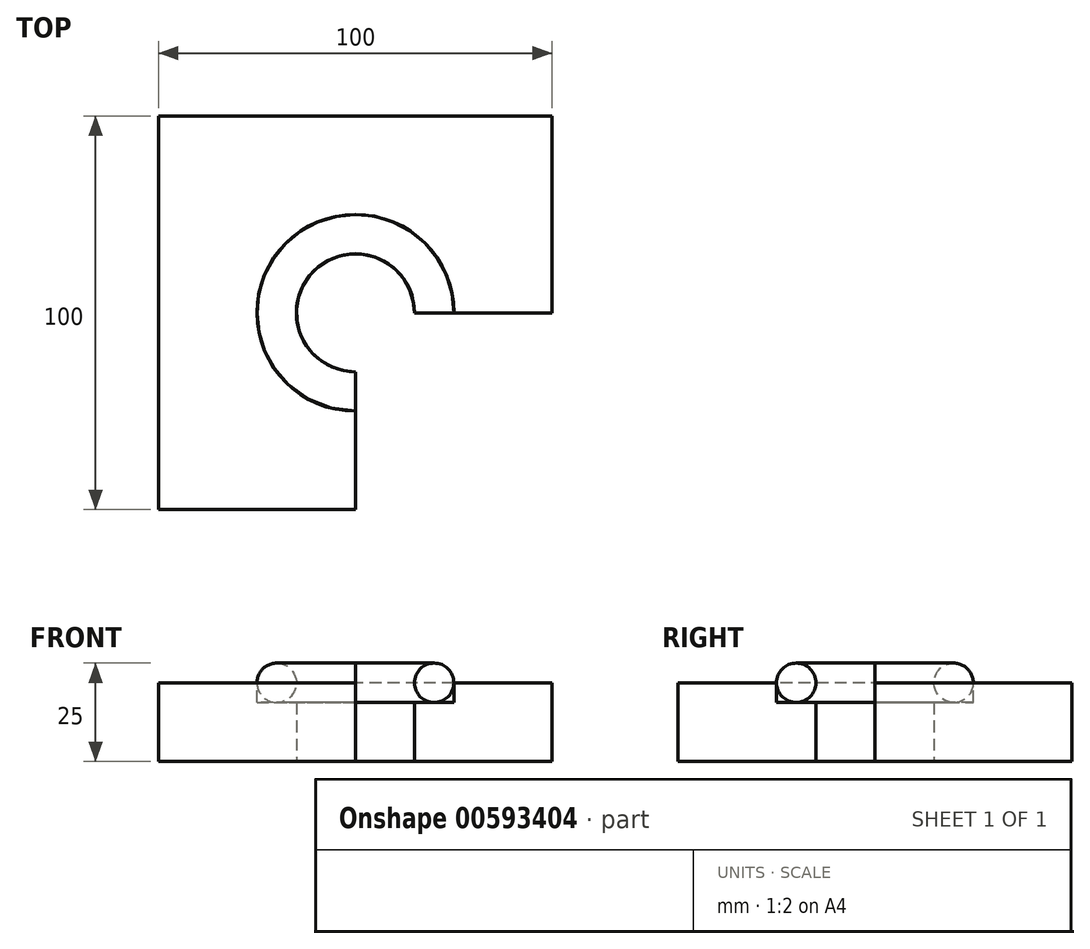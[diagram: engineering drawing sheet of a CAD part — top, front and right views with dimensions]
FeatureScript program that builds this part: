
annotation { "Feature Type Name" : "Feature", "Feature Type Description" : "" }
export const myFeature = defineFeature(function(context is Context, id is Id, definition is map)
    precondition{}
    {
        {
            var Q0;
            Q0=qCreatedBy(makeId("Top.planeOp"),FACE);
            var sketch = newSketch(context, id + "F0", { "sketchPlane" : qUnion([Q0])});
            skLineSegment(sketch, "E0.bottom", {"start": v(-50, 50) * mm, "end": v(50, 50) * mm});
            skLineSegment(sketch, "E0.top", {"start": v(-50, -50) * mm, "end": v(50, -50) * mm});
            skLineSegment(sketch, "E0.left", {"start": v(-50, 50) * mm, "end": v(-50, -50) * mm});
            skLineSegment(sketch, "E0.right", {"start": v(50, 50) * mm, "end": v(50, -50) * mm});
            skPoint(sketch, "E0.middle", {"position": v(0, 0) * mm});
            skCircle(sketch, "E1", {"center": v(0, 0) * mm, "radius": 15 * mm});
            skSolve(sketch);
        }
        {
            var Q0;
            Q0=makeQuery(id+"F0.imprint","IMPRINT",FACE,{"disambiguationData":[TD([[makeQuery(id+"F0.imprint","IMPRINT",EDGE,{"derivedFrom":sQuery(id+"F0.wireOp",EDGE,"E0.bottom")}),-1.0]])]});
            extrude(context, id + "F1", {"entities" : qUnion([Q0]), "depth" : 20 * mm, "offsetDistance" : 25 * mm});
        }
        {
            var Q0;
            Q0=makeQuery(id+"F1.opExtrude","CAP_FACE",FACE,{"disambiguationData":[OSD([sQuery(id+"F0.wireOp",EDGE,"E0.bottom"),sQuery(id+"F0.wireOp",EDGE,"E0.top"),sQuery(id+"F0.wireOp",EDGE,"E0.left"),sQuery(id+"F0.wireOp",EDGE,"E0.right"),sQuery(id+"F0.wireOp",EDGE,"E1")])],"isStart":false});
            var sketch = newSketch(context, id + "F2", { "sketchPlane" : qUnion([Q0])});
            skCircle(sketch, "E2", {"center": v(0, 0) * mm, "radius": 25 * mm});
            skSolve(sketch);
        }
        {
            var Q0;
            Q0=makeQuery(id+"F2.imprint","IMPRINT",FACE,{"disambiguationData":[TD([[makeQuery(id+"F2.imprint","IMPRINT",EDGE,{"derivedFrom":sQuery(id+"F2.wireOp",EDGE,"E2")}),1.0]])]});
            extrude(context, id + "F3", {"entities" : qUnion([Q0]), "operationType" : NewBodyOperationType.REMOVE, "oppositeDirection" : true, "depth" : 5 * mm, "offsetDistance" : 25 * mm});
        }
        {
            var Q0;
            Q0=qCreatedBy(makeId("Front.planeOp"),FACE);
            var sketch = newSketch(context, id + "F4", { "sketchPlane" : qUnion([Q0])});
            skCircle(sketch, "E3", {"center": v(-20, 20) * mm, "radius": 5 * mm});
            skSolve(sketch);
        }
        {
            var Q0;
            Q0 = qSketchRegion(id + "F4", true);
            var Q1;
            Q1=makeQuery(id+"F1.opExtrude","SWEPT_FACE",FACE,{"disambiguationData":[OSD([sQuery(id+"F0.wireOp",EDGE,"E1")])]});
            revolve(context, id + "F5", {"surfaceOperationType" : NewSurfaceOperationType.NEW, "entities" : qUnion([Q0]), "axis" : qUnion([Q1]), "revolveType" : RevolveType.FULL});
        }
        {
            var Q0;
            Q0=makeQuery(id+"F1.opExtrude","SWEPT_FACE",FACE,{"disambiguationData":[OSD([sQuery(id+"F0.wireOp",EDGE,"E0.top")])]});
            var sketch = newSketch(context, id + "F6", { "sketchPlane" : qUnion([Q0])});
            skLineSegment(sketch, "E4.bottom", {"start": v(50, 0) * mm, "end": v(0, 0) * mm});
            skLineSegment(sketch, "E4.top", {"start": v(50, 30) * mm, "end": v(0, 30) * mm});
            skLineSegment(sketch, "E4.left", {"start": v(50, 0) * mm, "end": v(50, 30) * mm});
            skLineSegment(sketch, "E4.right", {"start": v(0, 0) * mm, "end": v(0, 30) * mm});
            skSolve(sketch);
        }
        {
            var Q0;
            {var subQ0=sQuery(id+"F6.wireOp",EDGE,"E4.top");Q0=makeQuery(id+"F6.imprint","IMPRINT",FACE,{"disambiguationData":[TD([[makeQuery(id+"F6.imprint","IMPRINT",EDGE,{"derivedFrom":subQ0}),1.0]])]});}
            var Q1;
            {var subQ0=sQuery(id+"F6.wireOp",EDGE,"E4.bottom");Q1=makeQuery(id+"F6.imprint","IMPRINT",FACE,{"disambiguationData":[TD([[makeQuery(id+"F6.imprint","IMPRINT",EDGE,{"derivedFrom":subQ0}),1.0]])]});}
            extrude(context, id + "F7", {"entities" : qUnion([Q0, Q1]), "operationType" : NewBodyOperationType.REMOVE, "oppositeDirection" : true, "depth" : 50 * mm, "offsetDistance" : 25 * mm});
        }
    });
